# Revit family: Electronics_Commercial-Loudspeakers_Biamp_Passive-Loudspeaker_SDQ5P
name_source: partatom
category: Communication Devices
units: mm (PartAtom-declared; Revit-internal decimal feet)

## family parameters
Cut with Voids When Loaded = No
Host = Face
Maintain Annotation Orientation = No
OmniClass Number = 23.85.10.11.14.14.14
Part Type = Normal
Room Calculation Point = No
Round Connector Dimension = Use Diameter
Shared = No

## types (2) — shared parameters
Connector Description = Euroblock 2 pole; Speaker input
Depth = 6.38 "
Frequency response in Hz = 45-20k
Height = 9.96 "
Horizontal dispersion angle 1000 Hz = 180°
Loudspeaker system = 2-way
Low impedance RMS power in watts = 2 x 15
Low impedance dynamic power in watts = 2 x 30
Manufacturer = Biamp
Max SPL 1m in dB = 101
Mounting system = U-bracket
Product Documentation Link = https://downloads.biamp.com
Product Page URL = https://www.biamp.com
Product data url = https://bimobject.com
SPL 1W/1m in dB = 86
Tweeter size in inch = 1
URL = https://www.biamp.com
Vertical dispersion angle 1000 Hz = 180°
Weight = 12.90 lbf
Width = 7.09 "
Woofer cone material = Polypropylene
Woofer size in inch = 5.25
zero-valued in all types: Default Elevation

## per-type parameters (varying)
| type | Description | Grill Material | Housing Material | Mounting Material |
| SDQ5P B | SDQ5P-BL Active Loudspeaker Set 5", 2 x 30 Watts, Black | Biamp - Plastic - Black(Grid) | Biamp - Plastic - Black | Biamp - Metal - Black |
| SDQ5P W | SDQ5P-BL Active Loudspeaker Set 5", 2 x 30 Watts, White | Biamp - Plastic - White(Grid) | Biamp - Plastic - White | Biamp - Metal - White |

note: column(s) folded — value = type name in every type: Model

## geometry (parser evidence)
native form markers: Sweep x8
no freeform markers — native parametric forms only
